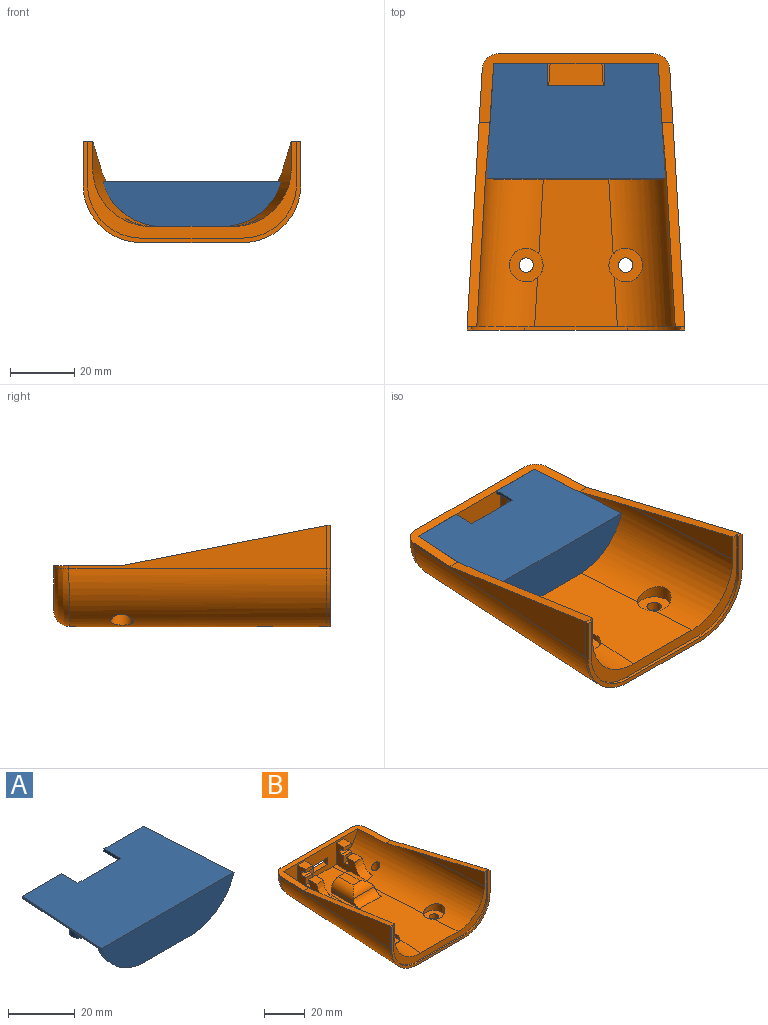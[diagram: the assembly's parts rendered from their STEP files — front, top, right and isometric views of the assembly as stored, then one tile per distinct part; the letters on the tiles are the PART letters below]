
ASSEMBLY  parts=2 mates=1
PART A: 22 faces, bbox 55.9x37.2x14 mm
  f0: plane 16.63x1mm, normal (0,1,0), area 16.5mm2, adj f1,f2,f4,f11
  f1: plane 55.85x36mm, normal (0,0,1), area 1801.8mm2, adj f0,f3,f4,f5,f6,f9,f10,f11
  f2: plane 54.94x33.82mm, normal (0,0,-1), area 1501.6mm2, adj f0,f3,f4,f5,f8,f9,f10,f11
  f3: plane 16.63x1mm, normal (0,1,0), area 16.5mm2, adj f1,f2,f5,f9
  f4: cylinder r=19.31mm len=37.2mm, axis (0.06,1,0), area 90.2mm2, adj f0,f1,f2,f6,f7,f8
  f5: cylinder r=19.31mm len=37.2mm, axis (0.06,-1,0), area 90.2mm2, adj f1,f2,f3,f6,f7,f8
  f6: plane 55.85x14mm, normal (0,-1,0), area 645mm2, adj f1,f4,f5,f7
  f7: plane 18.64x2.18mm, normal (0,0,-1), area 40.4mm2, adj f4,f5,f6,f8
  f8: plane 54.94x13mm, normal (0,1,0), area 585.8mm2, adj f2,f4,f5,f7
  f9: plane 7x1mm, normal (-1,0,0), area 7mm2, adj f1,f2,f3,f10
  f10: plane 18x1mm, normal (0,1,0), area 18mm2, adj f1,f2,f9,f11
  f11: plane 7x1mm, normal (1,0,0), area 7mm2, adj f0,f1,f2,f10
  f12: cylinder r=3mm len=6mm, axis (0,0,1), area 77.3mm2, adj f13,f21
  f13: plane 6x6mm, normal (0,0,-1), area 21.2mm2, adj f12,f19
  f14: cylinder r=3mm len=6mm, axis (0,0,1), area 77.3mm2, adj f15,f20
  f15: plane 6x6mm, normal (0,0,-1), area 21.2mm2, adj f14,f17
  f16: cone r=0mm half-angle=59deg, axis (0,0,-1), area 8.2mm2, adj f17
  f17: cylinder r=1.5mm len=4mm, axis (0,0,-1), area 37.7mm2, adj f15,f16
  f18: cone r=0mm half-angle=59deg, axis (0,0,-1), area 8.2mm2, adj f19
  f19: cylinder r=1.5mm len=4mm, axis (0,0,-1), area 37.7mm2, adj f13,f18
  f20: torus R=5mm, axis (0,0,-1), area 73.6mm2, adj f2,f14
  f21: torus R=5mm, axis (0,0,-1), area 73.6mm2, adj f2,f12
PART B: 89 faces, bbox 68.4x86.7x32.1 mm
  f0: cylinder r=18mm len=82.18mm, axis (0.06,-1,0), area 2220.1mm2, adj f22,f23,f25,f27,f40,f86
  f1: cylinder r=18mm len=82.18mm, axis (0.06,1,0), area 2217.9mm2, adj f20,f21,f25,f26,f39,f88
  f2: cylinder r=2mm len=5.2mm, axis (0,0,1), area 45.5mm2, adj f5,f87
  f3: cylinder r=2mm len=5.2mm, axis (0,0,1), area 45.5mm2, adj f4,f85
  f4: cylinder r=18mm len=84.18mm, axis (-0.06,1,0), area 2001.5mm2, adj f3,f10,f11,f18,f19,f24,f30,f31
  f5: cylinder r=18mm len=84.18mm, axis (-0.06,-1,0), area 2001.5mm2, adj f2,f8,f10,f11,f17,f19,f28,f29
  f6: plane 5x4.28mm, normal (0,-1,0), area 21.4mm2, adj f8,f51,f63,f74
  f7: plane 5x2mm, normal (0,-1,0), area 10mm2, adj f8,f51,f52,f65
  f8: plane 20.67x11.96mm, normal (-1,0,0), area 105mm2, adj f5,f6,f7,f10,f52,f63,f64,f65
  f9: plane 48.42x14.01mm, normal (0,1,0), area 565.9mm2, adj f14,f15,f16,f19,f21,f22,f44,f45
  f10: plane 51.47x14.18mm, normal (0,-1,0), area 431.6mm2, adj f4,f5,f8,f19,f31,f44,f45,f46
  f11: plane 65.48x30.53mm, normal (0,-1,0), area 340mm2, adj f4,f5,f24,f28,f29,f30,f31,f32
  f12: plane 10.5x10.5mm, normal (0,0,1), area 70.7mm2, adj f17,f20
  f13: plane 10.5x10.5mm, normal (0,0,1), area 70.7mm2, adj f18,f23
  f14: cylinder r=5mm len=4.99mm, axis (0,0,1), area 7.7mm2, adj f9,f19,f22,f27
  f15: cylinder r=5mm len=4.99mm, axis (0,0,-1), area 7.7mm2, adj f9,f19,f21,f26
  f16: cylinder r=5mm len=22.38mm, axis (1,0,0), area 175.8mm2, adj f9,f21,f22,f25
  f17: cylinder r=5.25mm len=10.5mm, axis (0,0,1), area 92.4mm2, adj f5,f12,f31
  f18: cylinder r=5.25mm len=10.5mm, axis (0,0,1), area 95.8mm2, adj f4,f13,f31
  f19: plane 60.37x21.45mm, normal (0,0,1), area 292.2mm2, adj f4,f5,f9,f10,f14,f15,f26,f27
  f20: cylinder r=2.25mm len=4.5mm, axis (0,0,1), area 42.4mm2, adj f1,f12,f25
  f21: bspline ~18.01x18mm, area 194.5mm2, adj f1,f9,f15,f16
  f22: bspline ~18.01x18mm, area 194.5mm2, adj f0,f9,f14,f16
  f23: cylinder r=2.25mm len=4.5mm, axis (0,0,1), area 41.3mm2, adj f0,f13,f25
  f24: plane 43.29x8.49mm, normal (-1,-0.06,0), area 184mm2, adj f4,f11,f30
  f25: plane 81.07x31.78mm, normal (0,0,-1), area 2190.6mm2, adj f0,f1,f16,f20,f23,f39,f40,f43
  f26: plane 80.36x13.49mm, normal (-1,0.06,0), area 479mm2, adj f1,f15,f19,f29,f38
  f27: plane 80.36x13.49mm, normal (1,0.06,0), area 479mm2, adj f0,f14,f19,f30,f41
  f28: plane 43.29x8.49mm, normal (1,-0.06,0), area 184mm2, adj f5,f11,f29
  f29: plane 63.74x12.59mm, normal (0,0.19,0.98), area 197.9mm2, adj f5,f11,f19,f26,f28,f37
  f30: plane 63.74x12.59mm, normal (0,0.19,0.98), area 197.9mm2, adj f4,f11,f19,f24,f27,f42
  f31: plane 82.07x25.77mm, normal (0,0,1), area 1411.3mm2, adj f4,f5,f10,f11,f17,f18,f53,f54
  f32: plane 13.49x1mm, normal (-1,0,0), area 13.5mm2, adj f11,f33,f42,f43
  f33: extruded ~16.63x16.6mm, area 26.1mm2, adj f11,f32,f34,f43
  f34: plane 31.78x1mm, normal (0,0,1), area 31.8mm2, adj f11,f33,f35,f43
  f35: extruded ~16.63x16.6mm, area 26.1mm2, adj f11,f34,f36,f43
  f36: plane 13.49x1mm, normal (1,0,0), area 13.5mm2, adj f11,f35,f37,f43
  f37: plane 1.4x1mm, normal (0,0,1), area 1.4mm2, adj f29,f36,f38,f43
  f38: plane 13.49x1mm, normal (-1,0,0), area 13.5mm2, adj f26,f37,f39,f43
  f39: extruded ~18.03x18mm, area 28.3mm2, adj f1,f25,f38,f43
  f40: extruded ~18.03x18mm, area 28.3mm2, adj f0,f25,f41,f43
  f41: plane 13.49x1mm, normal (1,0,0), area 13.5mm2, adj f27,f40,f42,f43
  f42: plane 1.4x1mm, normal (0,0,1), area 1.4mm2, adj f30,f32,f41,f43
  f43: plane 67.84x31.49mm, normal (0,-1,0), area 158.4mm2, adj f25,f32,f33,f34,f35,f36,f37,f38
  f44: plane 10x3mm, normal (0,0,-1), area 30mm2, adj f9,f10,f45,f47
  f45: plane 4x3mm, normal (-1,0,0), area 12mm2, adj f9,f10,f44,f46
  f46: plane 10x3mm, normal (0,0,1), area 30mm2, adj f9,f10,f45,f47
  f47: plane 4x3mm, normal (1,0,0), area 12mm2, adj f9,f10,f44,f46
  f48: plane 21.22x13.53mm, normal (-1,0,0), area 122.6mm2, adj f4,f10,f50,f66,f67,f68,f71,f72
  f49: plane 20.67x11.96mm, normal (1,0,0), area 105mm2, adj f4,f10,f50,f66,f67,f68,f71,f72
  f50: plane 5.5x5mm, normal (0,0,1), area 27.5mm2, adj f10,f48,f49,f82
  f51: plane 21.22x13.53mm, normal (1,0,0), area 122.6mm2, adj f5,f6,f7,f10,f52,f63,f64,f65
  f52: plane 5.5x5mm, normal (0,0,1), area 27.5mm2, adj f7,f8,f10,f51
  f53: plane 15x7mm, normal (0,1,0), area 72.7mm2, adj f31,f54,f55,f56,f57,f59,f60
  f54: plane 19.52x1.93mm, normal (-1,0,0), area 32.4mm2, adj f31,f53,f59,f62
  f55: plane 19.52x1.93mm, normal (1,0,0), area 32.4mm2, adj f31,f53,f60,f62
  f56: plane 9.93x4.86mm, normal (0,0,1), area 48.3mm2, adj f53,f59,f60,f61
  f57: cylinder r=2.6mm len=10mm, axis (0,1,0), area 163.4mm2, adj f53,f58
  f58: plane 5.2x5.2mm, normal (0,1,0), area 21.2mm2, adj f57
  f59: cylinder r=5.07mm len=15.57mm, axis (0,1,0), area 102.7mm2, adj f53,f54,f56,f61,f62
  f60: cylinder r=5.07mm len=15.57mm, axis (0,-1,0), area 102.7mm2, adj f53,f55,f56,f61,f62
  f61: cylinder r=5.07mm len=14.52mm, axis (-1,0,0), area 61.9mm2, adj f56,f59,f60,f62
  f62: cylinder r=5mm len=15mm, axis (-1,0,0), area 94.2mm2, adj f31,f54,f55,f59,f60,f61
  f63: plane 5x1.55mm, normal (0,0,1), area 7.8mm2, adj f6,f8,f51,f70
  f64: plane 5x0.1mm, normal (0,-1,0), area 0.5mm2, adj f8,f51,f69,f70
  f65: plane 5x1.55mm, normal (0,0,-1), area 7.8mm2, adj f7,f8,f51,f69
  f66: plane 5x1.55mm, normal (0,0,-1), area 7.8mm2, adj f48,f49,f71,f82
  f67: plane 5x0.1mm, normal (0,-1,0), area 0.5mm2, adj f48,f49,f71,f72
  f68: plane 5x1.55mm, normal (0,0,1), area 7.8mm2, adj f48,f49,f72,f78
  f69: cylinder r=1.45mm len=5mm, axis (1,0,0), area 11.4mm2, adj f8,f51,f64,f65
  f70: cylinder r=1.45mm len=5mm, axis (-1,0,0), area 11.4mm2, adj f8,f51,f63,f64
  f71: cylinder r=1.45mm len=5mm, axis (1,0,0), area 11.4mm2, adj f48,f49,f66,f67
  f72: cylinder r=1.45mm len=5mm, axis (-1,0,0), area 11.4mm2, adj f48,f49,f67,f68
  f73: plane 1.06x0.21mm, normal (0,-1,0), area 0.1mm2, adj f51,f76,f84
  f74: plane 5x3.62mm, normal (0,0,1), area 18.1mm2, adj f6,f8,f51,f75
  f75: plane 5x4.27mm, normal (0,0.91,-0.42), area 23.5mm2, adj f8,f51,f74,f76
  f76: plane 6.38x5.38mm, normal (0,0,1), area 29.3mm2, adj f8,f51,f73,f75,f84
  f77: plane 1.06x0.21mm, normal (0,-1,0), area 0.1mm2, adj f48,f79,f83
  f78: plane 5x4.28mm, normal (0,-1,0), area 21.4mm2, adj f48,f49,f68,f81
  f79: plane 6.38x5.38mm, normal (0,0,1), area 29.3mm2, adj f48,f49,f77,f80,f83
  f80: plane 5x4.27mm, normal (0,0.91,-0.42), area 23.5mm2, adj f48,f49,f79,f81
  f81: plane 5x3.62mm, normal (0,0,1), area 18.1mm2, adj f48,f49,f78,f80
  f82: plane 5x2mm, normal (0,-1,0), area 10mm2, adj f48,f49,f50,f66
  f83: bspline ~12.37x10.1mm, area 56.6mm2, adj f4,f48,f49,f77,f79
  f84: bspline ~12.37x10.1mm, area 56.6mm2, adj f5,f8,f51,f73,f76
  f85: cone r=0mm half-angle=59deg, axis (0,0,-1), area 30.2mm2, adj f3,f86
  f86: cylinder r=3.5mm len=7mm, axis (0,0,-1), area 46.3mm2, adj f0,f85
  f87: cone r=0mm half-angle=59deg, axis (0,0,-1), area 30.2mm2, adj f2,f88
  f88: cylinder r=3.5mm len=7mm, axis (0,0,-1), area 46.3mm2, adj f1,f87
PLACE A t=(-0.03,76.98,-43.99)mm
PLACE B t=(0,0,-1)mm
MATE fastened A.f1 <-> B.f19  axis (0,0,1) through (-25.65,97.07,-29.99)mm
